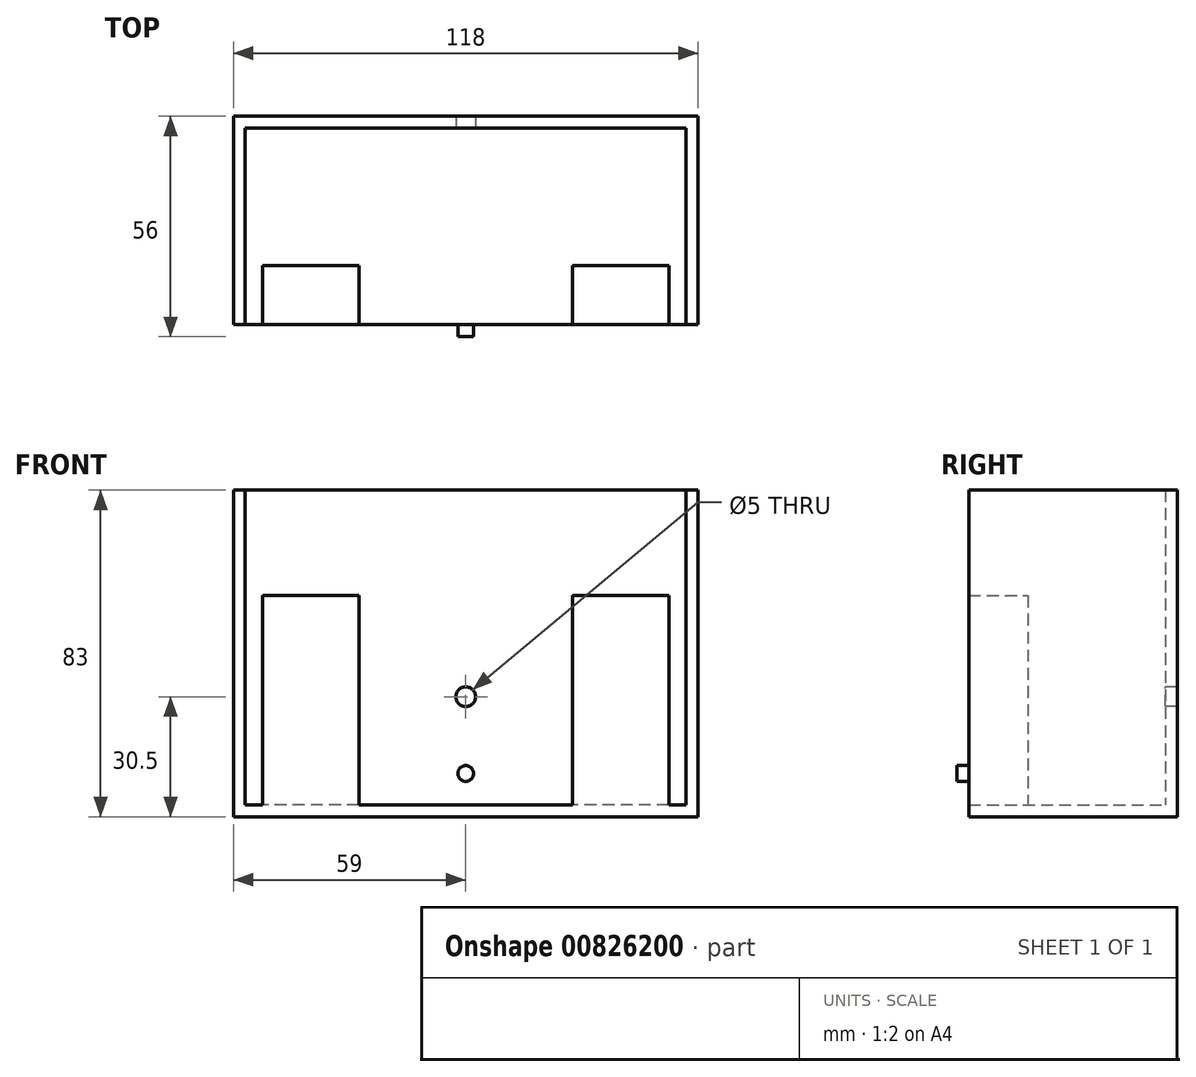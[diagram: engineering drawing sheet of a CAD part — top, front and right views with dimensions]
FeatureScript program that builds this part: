
annotation { "Feature Type Name" : "Feature", "Feature Type Description" : "" }
export const myFeature = defineFeature(function(context is Context, id is Id, definition is map)
    precondition{}
    {
        {
            var Q0;
            Q0=qCreatedBy(makeId("Top.planeOp"),FACE);
            var sketch = newSketch(context, id + "F0", { "sketchPlane" : qUnion([Q0])});
            skLineSegment(sketch, "E0.bottom", {"start": v(56, -25) * mm, "end": v(-56, -25) * mm});
            skLineSegment(sketch, "E0.top", {"start": v(56, 25) * mm, "end": v(-56, 25) * mm});
            skLineSegment(sketch, "E0.left", {"start": v(56, -25) * mm, "end": v(56, 25) * mm});
            skLineSegment(sketch, "E0.right", {"start": v(-56, -25) * mm, "end": v(-56, 25) * mm});
            skPoint(sketch, "E0.middle", {"position": v(0, 0) * mm});
            skLineSegment(sketch, "E1.bottom", {"start": v(59, -28) * mm, "end": v(-59, -28) * mm});
            skLineSegment(sketch, "E1.top", {"start": v(59, 28) * mm, "end": v(-59, 28) * mm});
            skLineSegment(sketch, "E1.left", {"start": v(59, -28) * mm, "end": v(59, 28) * mm});
            skLineSegment(sketch, "E1.right", {"start": v(-59, -28) * mm, "end": v(-59, 28) * mm});
            skSolve(sketch);
        }
        {
            var Q0;
            Q0=makeQuery(id+"F0.imprint","IMPRINT",FACE,{"disambiguationData":[TD([[makeQuery(id+"F0.imprint","IMPRINT",EDGE,{"derivedFrom":sQuery(id+"F0.wireOp",EDGE,"E0.bottom")}),-1.0]])]});
            extrude(context, id + "F1", {"entities" : qUnion([Q0]), "depth" : 3 * mm, "offsetDistance" : 25 * mm});
        }
        {
            var Q0;
            Q0=makeQuery(id+"F0.imprint","IMPRINT",FACE,{"disambiguationData":[TD([[makeQuery(id+"F0.imprint","IMPRINT",EDGE,{"derivedFrom":sQuery(id+"F0.wireOp",EDGE,"E0.bottom")}),1.0]])]});
            extrude(context, id + "F2", {"entities" : qUnion([Q0]), "operationType" : NewBodyOperationType.ADD, "depth" : 83 * mm, "offsetDistance" : 25 * mm});
        }
        {
            var Q0;
            Q0=makeQuery(id+"F2.opExtrude","SWEPT_FACE",FACE,{"disambiguationData":[OSD([sQuery(id+"F0.wireOp",EDGE,"E1.bottom")])]});
            var sketch = newSketch(context, id + "F3", { "sketchPlane" : qUnion([Q0])});
            skLineSegment(sketch, "E2", {"start": v(0, 0) * mm, "end": v(0, 55) * mm, "construction": true});
            skPoint(sketch, "E3", {"position": v(0, 6) * mm});
            skPoint(sketch, "E4", {"position": v(0, 16.5) * mm});
            skPoint(sketch, "E5", {"position": v(0, 44.5) * mm});
            skLineSegment(sketch, "E6.bottom", {"start": v(-24, 16.5) * mm, "end": v(24, 16.5) * mm});
            skLineSegment(sketch, "E6.top", {"start": v(-24, 44.5) * mm, "end": v(24, 44.5) * mm});
            skLineSegment(sketch, "E6.left", {"start": v(-24, 16.5) * mm, "end": v(-24, 44.5) * mm});
            skLineSegment(sketch, "E6.right", {"start": v(24, 16.5) * mm, "end": v(24, 44.5) * mm});
            skPoint(sketch, "E7", {"position": v(0, 55) * mm});
            skPoint(sketch, "E8", {"position": v(0, 52) * mm});
            skPoint(sketch, "E9", {"position": v(0, 30.5) * mm});
            skLineSegment(sketch, "E10", {"start": v(0, 55) * mm, "end": v(0, 6) * mm, "construction": true});
            skLineSegment(sketch, "E11", {"start": v(-41.18, 30.5) * mm, "end": v(52.47, 30.5) * mm, "construction": true});
            skCircle(sketch, "E12", {"center": v(0, 50) * mm, "radius": 2 * mm});
            skCircle(sketch, "E13.MirrorC", {"center": v(0, 11) * mm, "radius": 2 * mm});
            skCircle(sketch, "E14", {"center": v(0, 30.5) * mm, "radius": 2.5 * mm});
            skSolve(sketch);
        }
        {
            var Q0;
            Q0=makeQuery(id+"F3.imprint","IMPRINT",FACE,{"disambiguationData":[TD([[makeQuery(id+"F3.imprint","IMPRINT",EDGE,{"derivedFrom":sQuery(id+"F3.wireOp",EDGE,"E6.bottom")}),1.0]])]});
            var Q1;
            Q1=makeQuery(id+"F3.imprint","IMPRINT",FACE,{"disambiguationData":[TD([[makeQuery(id+"F3.imprint","IMPRINT",EDGE,{"derivedFrom":sQuery(id+"F3.wireOp",EDGE,"E14")}),1.0]])]});
            extrude(context, id + "F4", {"entities" : qUnion([Q0, Q1]), "operationType" : NewBodyOperationType.REMOVE, "oppositeDirection" : true, "depth" : 3 * mm, "offsetDistance" : 25 * mm});
        }
        {
            var Q0;
            Q0=makeQuery(id+"F3.imprint","IMPRINT",FACE,{"disambiguationData":[TD([[makeQuery(id+"F3.imprint","IMPRINT",EDGE,{"derivedFrom":sQuery(id+"F3.wireOp",EDGE,"E12")}),1.0]])]});
            var Q1;
            Q1=makeQuery(id+"F3.imprint","IMPRINT",FACE,{"disambiguationData":[TD([[makeQuery(id+"F3.imprint","IMPRINT",EDGE,{"derivedFrom":sQuery(id+"F3.wireOp",EDGE,"E13.MirrorC")}),-1.0]])]});
            extrude(context, id + "F5", {"entities" : qUnion([Q0, Q1]), "operationType" : NewBodyOperationType.REMOVE, "oppositeDirection" : true, "depth" : 3 * mm, "offsetDistance" : 25 * mm});
        }
        {
            var Q0;
            Q0=makeQuery(id+"F3.imprint","IMPRINT",FACE,{"disambiguationData":[TD([[makeQuery(id+"F3.imprint","IMPRINT",EDGE,{"derivedFrom":sQuery(id+"F3.wireOp",EDGE,"E14")}),1.0]])]});
            extrude(context, id + "F6", {"entities" : qUnion([Q0]), "operationType" : NewBodyOperationType.REMOVE, "oppositeDirection" : true, "depth" : 76.6 * mm, "offsetDistance" : 25 * mm});
        }
        {
            var Q0;
            Q0=makeQuery(id+"F1.opExtrude","CAP_FACE",FACE,{"disambiguationData":[OSD([sQuery(id+"F0.wireOp",EDGE,"E0.bottom"),sQuery(id+"F0.wireOp",EDGE,"E0.top"),sQuery(id+"F0.wireOp",EDGE,"E0.left"),sQuery(id+"F0.wireOp",EDGE,"E0.right")])],"isStart":false});
            var sketch = newSketch(context, id + "F7", { "sketchPlane" : qUnion([Q0])});
            skLineSegment(sketch, "E15.bottom", {"start": v(-51.59, -25) * mm, "end": v(-27.13, -25) * mm});
            skLineSegment(sketch, "E15.top", {"start": v(-51.59, -10) * mm, "end": v(-27.13, -10) * mm});
            skLineSegment(sketch, "E15.left", {"start": v(-51.59, -25) * mm, "end": v(-51.59, -10) * mm});
            skLineSegment(sketch, "E15.right", {"start": v(-27.13, -25) * mm, "end": v(-27.13, -10) * mm});
            skLineSegment(sketch, "E16.MirrorCS", {"start": v(27.13, -25) * mm, "end": v(27.13, -10) * mm});
            skLineSegment(sketch, "E17.MirrorCS", {"start": v(51.59, -10) * mm, "end": v(27.13, -10) * mm});
            skLineSegment(sketch, "E18.MirrorCS", {"start": v(51.59, -25) * mm, "end": v(51.59, -10) * mm});
            skLineSegment(sketch, "E19.MirrorCS", {"start": v(51.59, -25) * mm, "end": v(27.13, -25) * mm});
            skSolve(sketch);
        }
        {
            var Q0;
            Q0=makeQuery(id+"F7.imprint","IMPRINT",FACE,{"disambiguationData":[TD([[makeQuery(id+"F7.imprint","IMPRINT",EDGE,{"derivedFrom":sQuery(id+"F7.wireOp",EDGE,"E15.bottom")}),-1.0]])]});
            var Q1;
            Q1=makeQuery(id+"F7.imprint","IMPRINT",FACE,{"disambiguationData":[TD([[makeQuery(id+"F7.imprint","IMPRINT",EDGE,{"derivedFrom":sQuery(id+"F7.wireOp",EDGE,"E16.MirrorCS")}),-1.0]])]});
            extrude(context, id + "F8", {"entities" : qUnion([Q0, Q1]), "operationType" : NewBodyOperationType.ADD, "depth" : 53.2 * mm, "offsetDistance" : 25 * mm});
        }
    });
